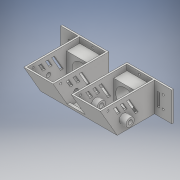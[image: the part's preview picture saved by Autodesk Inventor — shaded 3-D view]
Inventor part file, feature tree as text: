
AUTODESK INVENTOR PART (.ipt)
format: ipt  version: 2018.2 (Build 222227000, 227)  size: 413,696 bytes
history: native  units: mm
features: extrude x24, sketch x24
ambient origin geometry x8: Origin, YZ Plane, XZ Plane, XY Plane, X Axis, Y Axis, Z Axis, Center Point
bodies: Solid1 (feature_tree)
feature tree (48):
  extrude  "Extrusion1"  Depth=56.0mm
  extrude  "Extrusion2"  Depth=2.4mm
  extrude  "Extrusion3"  Depth=2.4mm
  extrude  "Extrusion4"  Depth=2.4mm
  sketch  "Sketch5"  dims[d9=2.4mm d10=39.6mm d11=0.0mm]
  extrude  "Extrusion5"  Depth=39.6mm TaperAngle=0.0deg
  extrude  "Extrusion6"  Depth=13.0mm
  extrude  "Extrusion7"  Depth=2.4mm
  extrude  "Extrusion8"  Depth=39.6mm TaperAngle=0.0deg
  extrude  "Extrusion9"  Depth=3.0mm
  extrude  "Extrusion10"  Depth=12.0mm
  extrude  "Extrusion11"  Depth=19.0mm
  extrude  "Extrusion12"  Depth=45.0mm
  extrude  "Extrusion13"  Depth=12.0mm
  extrude  "Extrusion21"  Depth=12.0mm
  extrude  "Extrusion22"  Depth=12.0mm
  extrude  "Extrusion23"  Depth=12.0mm
  extrude  "Extrusion24"  Depth=8.0mm
  extrude  "Extrusion25"  Depth=16.0mm
  extrude  "Extrusion26"  Depth=25.0mm
  extrude  "Extrusion27"  Depth=23.0mm TaperAngle=0.0deg
  extrude  "Extrusion28"  Depth=3.0mm
  extrude  "Extrusion29"  Depth=12.5mm
  extrude  "Extrusion30"  Depth=20.0mm TaperAngle=0.0deg
  extrude  "Extrusion31"  Depth=3.0mm
  sketch  "Sketch1"  dims[d0=110.0mm d1=56.0mm]
  sketch  "Sketch2"  dims[d2=25.0mm d3=2.4mm]
  sketch  "Sketch3"  dims[d4=25.0mm d5=2.4mm]
  sketch  "Sketch4"  dims[d6=42.0mm d7=0.0mm d8=2.4mm]
  sketch  "Sketch6"  dims[d12=13.0mm d13=13.0mm]
  sketch  "Sketch7"  dims[d14=39.6mm d15=0.0mm d16=2.4mm]
  sketch  "Sketch8"  dims[d17=2.4mm d18=39.6mm d19=0.0mm]
  sketch  "Sketch9"  dims[d20=3.0mm d21=3.0mm]
  sketch  "Sketch10"  dims[d22=12.0mm d23=12.0mm]
  sketch  "Sketch11"  dims[d24=19.0mm d25=0.0mm d26=6.3mm]
  sketch  "Sketch12"  dims[d27=17.0mm d28=45.0mm]
  sketch  "Sketch13"  dims[d29=110.0mm d30=0.0mm d31=12.0mm]
  sketch  "Sketch21"  dims[d32=10.0mm d33=0.0mm d34=12.0mm]
  sketch  "Sketch22"  dims[d35=8.0mm d36=0.0mm d37=12.0mm]
  sketch  "Sketch23"  dims[d38=10.0mm d39=0.0mm d40=12.0mm]
  sketch  "Sketch24"  dims[d41=8.0mm d42=0.0mm d43=26.5mm]
  sketch  "Sketch25"  dims[d44=26.5mm d45=16.0mm]
  sketch  "Sketch26"  dims[d46=16.0mm d47=25.0mm]
  sketch  "Sketch27"  dims[d48=25.0mm d49=23.0mm d50=0.0mm]
  sketch  "Sketch28"  dims[d51=3.0mm d52=3.0mm]
  sketch  "Sketch29"  dims[d53=12.5mm d54=12.5mm]
  sketch  "Sketch31"  dims[d55=12.5mm d56=20.0mm d57=0.0mm]
  sketch  "Sketch32"  dims[d58=3.0mm d59=3.0mm d60=6.5mm d61=6.5mm d62=20.0mm d63=0.0mm d84=30.0deg d85=2.4mm d86=0.0mm d87=30.0deg d88=2.4mm d89=0.0mm d90=30.0deg d91=2.4mm d92=0.0mm d93=30.0deg d94=2.4mm d95=0.0mm d96=2.4mm d97=38.0mm d98=0.0mm d99=2.4mm d100=38.0mm d101=0.0mm d102=7.0mm d103=90.0deg d104=26.0mm d105=0.0mm d106=3.0mm d107=5.0mm d108=7.0mm d109=120.0mm d110=0.0mm d111=4.0mm d112=10.0mm d113=4.0mm d114=4.0mm d115=10.0mm d116=6.0mm d117=6.0mm d118=5.0mm d119=4.0mm d120=4.0mm d121=5.0mm d122=6.0mm d123=120.0mm d124=0.0mm d125=8.0mm d126=0.0mm d127=3.0mm d128=3.0mm d129=4.0mm d130=4.0mm d131=18.0mm d132=18.0mm d133=8.0mm d134=0.0mm]
